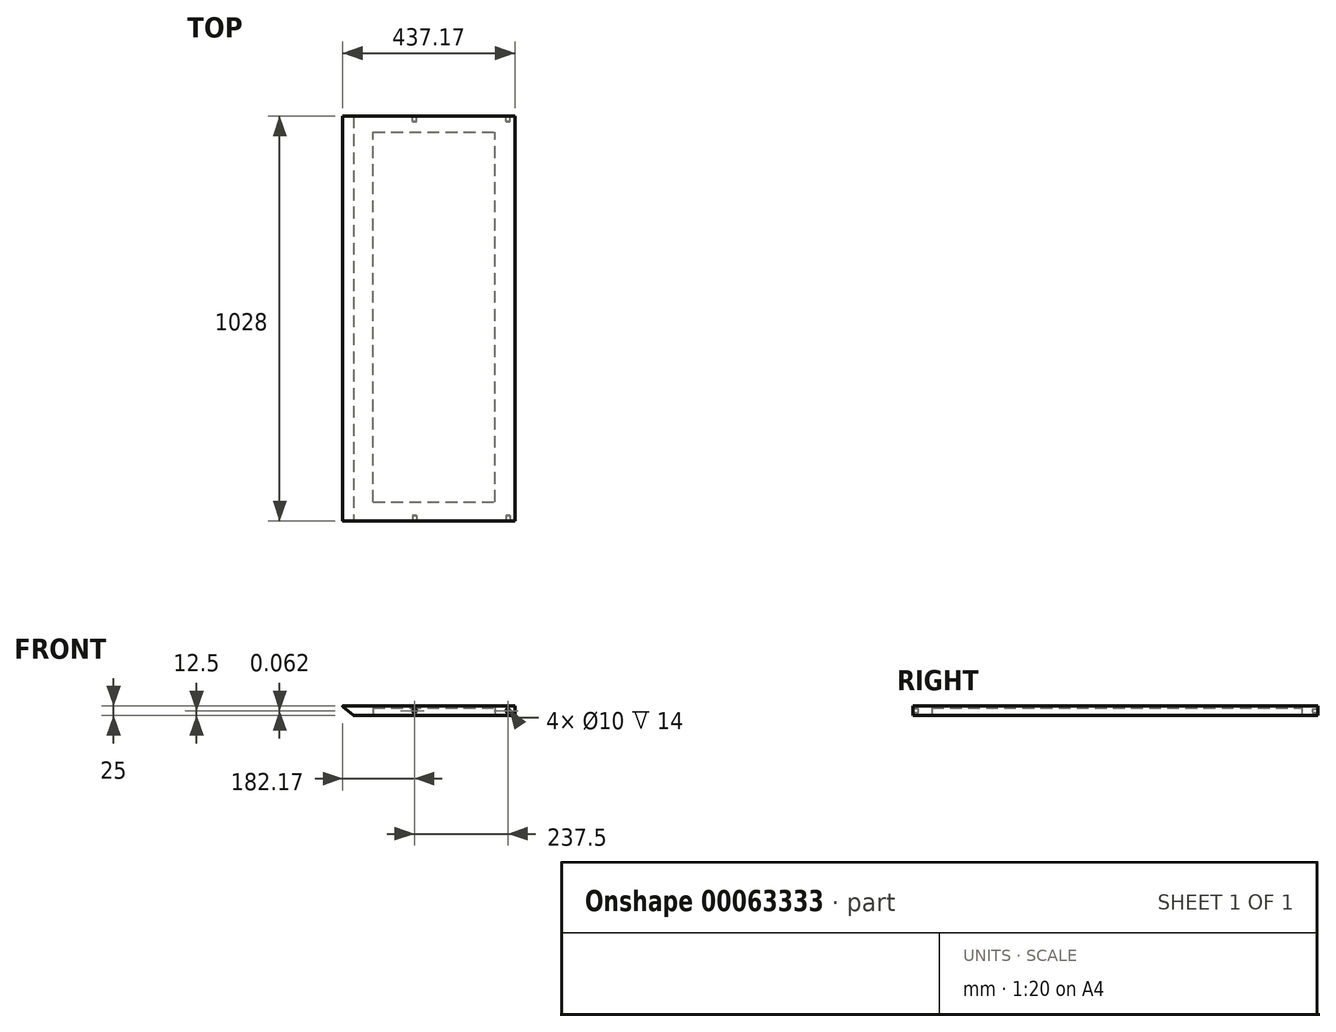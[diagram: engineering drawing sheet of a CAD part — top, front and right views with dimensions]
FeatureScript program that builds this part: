
annotation { "Feature Type Name" : "Feature", "Feature Type Description" : "" }
export const myFeature = defineFeature(function(context is Context, id is Id, definition is map)
    precondition{}
    {
        {
            var Q0;
            Q0=qCreatedBy(makeId("Top.planeOp"),FACE);
            var sketch = newSketch(context, id + "F0", { "sketchPlane" : qUnion([Q0])});
            skLineSegment(sketch, "E0.rect.bottom", {"start": v(205, 514) * mm, "end": v(-205, 514) * mm});
            skLineSegment(sketch, "E0.rect.top", {"start": v(205, -514) * mm, "end": v(-205, -514) * mm});
            skLineSegment(sketch, "E0.rect.left", {"start": v(205, 514) * mm, "end": v(205, -514) * mm});
            skLineSegment(sketch, "E0.rect.right", {"start": v(-205, 514) * mm, "end": v(-205, -514) * mm});
            skPoint(sketch, "E0.rect.middle", {"position": v(0, 0) * mm});
            skSolve(sketch);
        }
        {
            var Q0;
            Q0=makeQuery(id+"F0.imprint","IMPRINT",FACE,{"disambiguationData":[TD([[makeQuery(id+"F0.imprint","IMPRINT",EDGE,{"derivedFrom":sQuery(id+"F0.wireOp",EDGE,"E0.rect.bottom")}),1.0]])]});
            extrude(context, id + "F1", {"entities" : qUnion([Q0]), "depth" : 25 * mm});
        }
        {
            var Q0;
            Q0=makeQuery(id+"F1.opExtrude","SWEPT_FACE",FACE,{"disambiguationData":[OSD([sQuery(id+"F0.wireOp",EDGE,"E0.rect.top")])]});
            var sketch = newSketch(context, id + "F2", { "sketchPlane" : qUnion([Q0])});
            skCircle(sketch, "E1", {"center": v(187.5, 12.5) * mm, "radius": 5 * mm});
            skCircle(sketch, "E2", {"center": v(-50, 12.5) * mm, "radius": 5 * mm});
            skSolve(sketch);
        }
        {
            var Q0;
            Q0=makeQuery(id+"F2.imprint","IMPRINT",FACE,{"disambiguationData":[TD([[makeQuery(id+"F2.imprint","IMPRINT",EDGE,{"derivedFrom":sQuery(id+"F2.wireOp",EDGE,"E1")}),1.0]])]});
            var Q1;
            Q1=makeQuery(id+"F2.imprint","IMPRINT",FACE,{"disambiguationData":[TD([[makeQuery(id+"F2.imprint","IMPRINT",EDGE,{"derivedFrom":sQuery(id+"F2.wireOp",EDGE,"E2")}),1.0]])]});
            extrude(context, id + "F3", {"entities" : qUnion([Q0, Q1]), "operationType" : NewBodyOperationType.REMOVE, "oppositeDirection" : true, "depth" : 14 * mm});
        }
        {
            var Q0;
            Q0=makeQuery(id+"F1.opExtrude","SWEPT_FACE",FACE,{"disambiguationData":[OSD([sQuery(id+"F0.wireOp",EDGE,"E0.rect.bottom")])]});
            var sketch = newSketch(context, id + "F4", { "sketchPlane" : qUnion([Q0])});
            skCircle(sketch, "E3", {"center": v(-187.5, 12.56) * mm, "radius": 5 * mm});
            skCircle(sketch, "E4", {"center": v(50, 12.56) * mm, "radius": 5 * mm});
            skSolve(sketch);
        }
        {
            var Q0;
            Q0=makeQuery(id+"F4.imprint","IMPRINT",FACE,{"disambiguationData":[TD([[makeQuery(id+"F4.imprint","IMPRINT",EDGE,{"derivedFrom":sQuery(id+"F4.wireOp",EDGE,"E3")}),1.0]])]});
            var Q1;
            Q1=makeQuery(id+"F4.imprint","IMPRINT",FACE,{"disambiguationData":[TD([[makeQuery(id+"F4.imprint","IMPRINT",EDGE,{"derivedFrom":sQuery(id+"F4.wireOp",EDGE,"E4")}),1.0]])]});
            extrude(context, id + "F5", {"entities" : qUnion([Q0, Q1]), "operationType" : NewBodyOperationType.REMOVE, "oppositeDirection" : true, "depth" : 14 * mm});
        }
        {
            var Q0;
            Q0=makeQuery(id+"F1.opExtrude","SWEPT_FACE",FACE,{"disambiguationData":[OSD([sQuery(id+"F0.wireOp",EDGE,"E0.rect.top")])]});
            var sketch = newSketch(context, id + "F6", { "sketchPlane" : qUnion([Q0])});
            skLineSegment(sketch, "E5", {"start": v(-205, 25) * mm, "end": v(-230.67, 25) * mm});
            skLineSegment(sketch, "E6", {"start": v(-231.64, 22.35) * mm, "end": v(-206.4, 1.17) * mm});
            skLineSegment(sketch, "E7", {"start": v(-205, 0) * mm, "end": v(-205, 25) * mm});
            skPoint(sketch, "E8.visualSharp", {"position": v(-234.8, 25) * mm});
            skArc(sketch, "E8.filletArc", {"start": v(-230.67, 25) * mm, "mid": v(-232.08, 24.01) * mm, "end": v(-231.64, 22.35) * mm});
            skLineSegment(sketch, "E9", {"start": v(-203.18, 0) * mm, "end": v(-160.5, 0) * mm});
            skPoint(sketch, "E10.visualSharp", {"position": v(-205, 0) * mm});
            skArc(sketch, "E10.filletArc", {"start": v(-206.4, 1.17) * mm, "mid": v(-204.9, 0.3) * mm, "end": v(-203.18, 0) * mm});
            skSolve(sketch);
        }
        {
            var Q0;
            {var subQ1=sQuery(id+"F6.wireOp",EDGE,"E5");Q0=makeQuery(id+"F6.imprint","IMPRINT",FACE,{"disambiguationData":[TD([[makeQuery(id+"F6.imprint","IMPRINT",EDGE,{"derivedFrom":subQ1}),1.0]])]});}
            extrude(context, id + "F7", {"entities" : qUnion([Q0]), "operationType" : NewBodyOperationType.ADD, "oppositeDirection" : true, "depth" : 1028 * mm});
        }
        {
            var Q0;
            Q0=makeQuery(id+"F1.opExtrude","CAP_FACE",FACE,{"disambiguationData":[OSD([sQuery(id+"F0.wireOp",EDGE,"E0.rect.bottom"),sQuery(id+"F0.wireOp",EDGE,"E0.rect.top"),sQuery(id+"F0.wireOp",EDGE,"E0.rect.left"),sQuery(id+"F0.wireOp",EDGE,"E0.rect.right")])],"isStart":true});
            var sketch = newSketch(context, id + "F8", { "sketchPlane" : qUnion([Q0])});
            skLineSegment(sketch, "E11.bottom", {"start": v(-155, 466) * mm, "end": v(155, 466) * mm});
            skLineSegment(sketch, "E11.top", {"start": v(-155, -474) * mm, "end": v(155, -474) * mm});
            skLineSegment(sketch, "E11.left", {"start": v(-155, 466) * mm, "end": v(-155, -474) * mm});
            skLineSegment(sketch, "E11.right", {"start": v(155, 466) * mm, "end": v(155, -474) * mm});
            skSolve(sketch);
        }
        {
            var Q0;
            Q0=makeQuery(id+"F8.imprint","IMPRINT",FACE,{"disambiguationData":[TD([[makeQuery(id+"F8.imprint","IMPRINT",EDGE,{"derivedFrom":sQuery(id+"F8.wireOp",EDGE,"E11.bottom")}),-1.0]])]});
            extrude(context, id + "F9", {"entities" : qUnion([Q0]), "operationType" : NewBodyOperationType.REMOVE, "oppositeDirection" : true, "depth" : 19 * mm});
        }
    });
